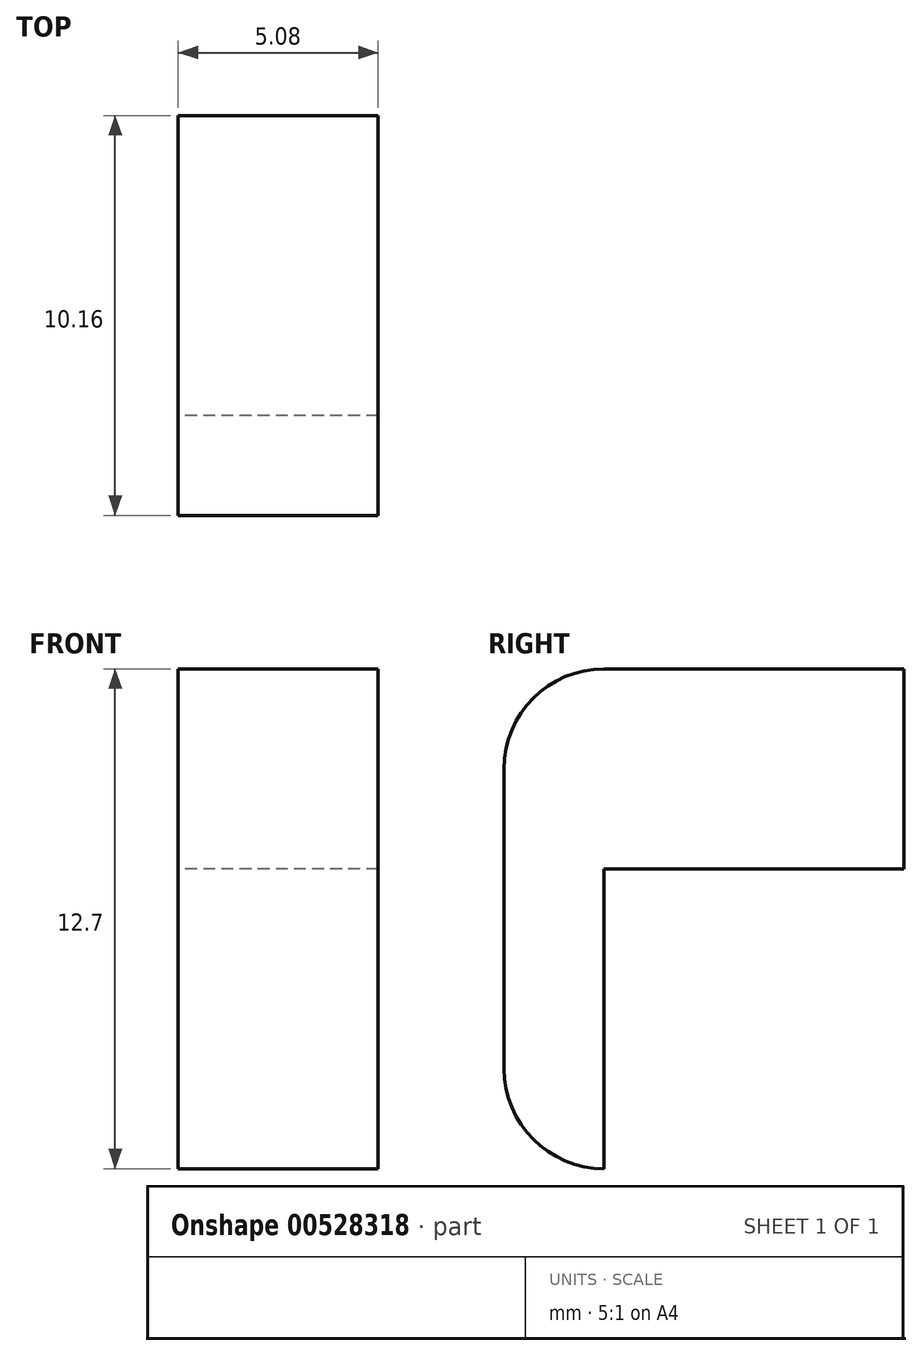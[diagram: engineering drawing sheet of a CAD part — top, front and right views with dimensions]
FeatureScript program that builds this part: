
annotation { "Feature Type Name" : "Feature", "Feature Type Description" : "" }
export const myFeature = defineFeature(function(context is Context, id is Id, definition is map)
    precondition{}
    {
        {
            var Q0;
            Q0=qCreatedBy(makeId("Front.planeOp"),FACE);
            var sketch = newSketch(context, id + "F0", { "sketchPlane" : qUnion([Q0])});
            skLineSegment(sketch, "E0.bottom", {"start": v(2.54, 2.54) * mm, "end": v(-2.54, 2.54) * mm});
            skLineSegment(sketch, "E0.top", {"start": v(2.54, -2.54) * mm, "end": v(-2.54, -2.54) * mm});
            skLineSegment(sketch, "E0.left", {"start": v(2.54, 2.54) * mm, "end": v(2.54, -2.54) * mm});
            skLineSegment(sketch, "E0.right", {"start": v(-2.54, 2.54) * mm, "end": v(-2.54, -2.54) * mm});
            skPoint(sketch, "E0.middle", {"position": v(0, 0) * mm});
            skSolve(sketch);
        }
        {
            var Q0;
            Q0 = qSketchRegion(id + "F0", true);
            extrude(context, id + "F1", {"entities" : qUnion([Q0]), "depth" : 7.62 * mm, "offsetDistance" : 25.4 * mm});
        }
        {
            var Q0;
            Q0=makeQuery(id+"F1.opExtrude","CAP_FACE",FACE,{"disambiguationData":[OSD([sQuery(id+"F0.wireOp",EDGE,"E0.bottom"),sQuery(id+"F0.wireOp",EDGE,"E0.top"),sQuery(id+"F0.wireOp",EDGE,"E0.left"),sQuery(id+"F0.wireOp",EDGE,"E0.right")])],"isStart":false});
            var sketch = newSketch(context, id + "F2", { "sketchPlane" : qUnion([Q0])});
            skLineSegment(sketch, "E1.bottom", {"start": v(-2.54, 2.54) * mm, "end": v(2.54, 2.54) * mm});
            skLineSegment(sketch, "E1.top", {"start": v(-2.54, -10.16) * mm, "end": v(2.54, -10.16) * mm});
            skLineSegment(sketch, "E1.left", {"start": v(-2.54, 2.54) * mm, "end": v(-2.54, -10.16) * mm});
            skLineSegment(sketch, "E1.right", {"start": v(2.54, 2.54) * mm, "end": v(2.54, -10.16) * mm});
            skSolve(sketch);
        }
        {
            var Q0;
            Q0 = qSketchRegion(id + "F2", true);
            extrude(context, id + "F3", {"entities" : qUnion([Q0]), "operationType" : NewBodyOperationType.ADD, "depth" : 2.54 * mm, "offsetDistance" : 25.4 * mm});
        }
        {
            var Q0;
            Q0=makeQuery(id+"F3.opExtrude","CAP_EDGE",EDGE,{"disambiguationData":[OSD([sQuery(id+"F2.wireOp",EDGE,"E1.bottom")])],"isStart":false});
            var Q1;
            Q1=makeQuery(id+"F3.opExtrude","CAP_EDGE",EDGE,{"disambiguationData":[OSD([sQuery(id+"F2.wireOp",EDGE,"E1.top")])],"isStart":false});
            fillet(context, id + "F4", {"entities" : qUnion([Q0, Q1]), "radius" : 2.54 * mm, "tangentPropagation" : true, "allowEdgeOverflow" : false});
        }
    });
